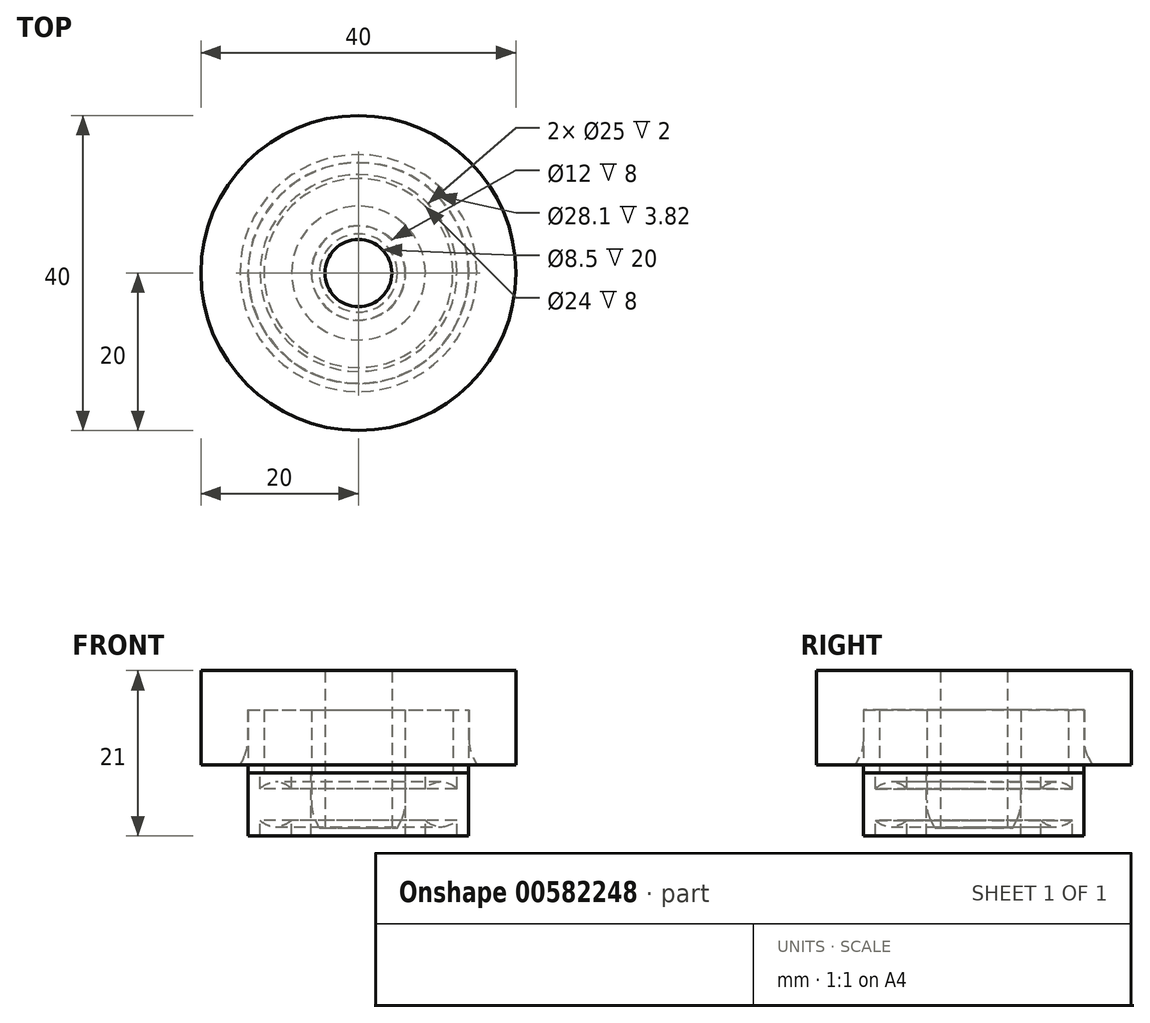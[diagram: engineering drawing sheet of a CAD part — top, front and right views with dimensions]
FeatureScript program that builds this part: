
annotation { "Feature Type Name" : "Feature", "Feature Type Description" : "" }
export const myFeature = defineFeature(function(context is Context, id is Id, definition is map)
    precondition{}
    {
        {
            var Q0;
            Q0=qCreatedBy(makeId("Front.planeOp"),FACE);
            var sketch = newSketch(context, id + "F0", { "sketchPlane" : qUnion([Q0])});
            skLineSegment(sketch, "E0", {"start": v(0, 0) * mm, "end": v(0, 32.04) * mm, "construction": true});
            skLineSegment(sketch, "E1.bottom", {"start": v(12, 0) * mm, "end": v(14, 0) * mm});
            skLineSegment(sketch, "E1.top", {"start": v(12, 8) * mm, "end": v(14, 8) * mm});
            skLineSegment(sketch, "E1.left", {"start": v(12, 0) * mm, "end": v(12, 8) * mm});
            skLineSegment(sketch, "E1.right", {"start": v(14, 0) * mm, "end": v(14, 8) * mm});
            skSolve(sketch);
        }
        {
            var Q0;
            Q0 = qSketchRegion(id + "F0", true);
            var Q1;
            Q1=sQuery(id+"F0.wireOp",EDGE,"E0");
            revolve(context, id + "F1", {"entities" : qUnion([Q0]), "axis" : qUnion([Q1]), "revolveType" : RevolveType.FULL});
        }
        {
            var Q0;
            Q0=qCreatedBy(makeId("Front.planeOp"),FACE);
            var sketch = newSketch(context, id + "F2", { "sketchPlane" : qUnion([Q0])});
            skLineSegment(sketch, "E2", {"start": v(0, 0) * mm, "end": v(0, 16.36) * mm, "construction": true});
            skLineSegment(sketch, "E3", {"start": v(14.05, 1) * mm, "end": v(20, 1) * mm});
            skLineSegment(sketch, "E4", {"start": v(20, 1) * mm, "end": v(20, 13) * mm});
            skLineSegment(sketch, "E5", {"start": v(20, 13) * mm, "end": v(4.25, 13) * mm});
            skLineSegment(sketch, "E6", {"start": v(4.25, 13) * mm, "end": v(4.25, -7) * mm});
            skLineSegment(sketch, "E7", {"start": v(4.25, -7) * mm, "end": v(5.95, -7) * mm});
            skLineSegment(sketch, "E8", {"start": v(5.95, -7) * mm, "end": v(5.95, 8) * mm});
            skLineSegment(sketch, "E9", {"start": v(5.95, 8) * mm, "end": v(14.05, 8) * mm});
            skLineSegment(sketch, "E10", {"start": v(14.05, 8) * mm, "end": v(14.05, 1) * mm});
            skSolve(sketch);
        }
        {
            var Q0;
            Q0 = qSketchRegion(id + "F2", true);
            var Q1;
            Q1=sQuery(id+"F2.wireOp",EDGE,"E2");
            revolve(context, id + "F3", {"entities" : qUnion([Q0]), "axis" : qUnion([Q1]), "revolveType" : RevolveType.FULL});
        }
        {
            var Q0;
            Q0=qCreatedBy(makeId("Front.planeOp"),FACE);
            var sketch = newSketch(context, id + "F4", { "sketchPlane" : qUnion([Q0])});
            skLineSegment(sketch, "E11", {"start": v(0, 0) * mm, "end": v(0, -20.8) * mm, "construction": true});
            skLineSegment(sketch, "E12", {"start": v(14, 0) * mm, "end": v(14, -8) * mm});
            skLineSegment(sketch, "E13", {"start": v(14, -8) * mm, "end": v(12.5, -8) * mm});
            skLineSegment(sketch, "E14", {"start": v(12.5, -8) * mm, "end": v(12.5, -6) * mm});
            skLineSegment(sketch, "E15", {"start": v(12.5, -6) * mm, "end": v(8.5, -6) * mm, "construction": true});
            skLineSegment(sketch, "E16", {"start": v(8.5, -6) * mm, "end": v(8.5, -8) * mm});
            skLineSegment(sketch, "E17", {"start": v(8.5, -8) * mm, "end": v(6, -8) * mm});
            skLineSegment(sketch, "E18", {"start": v(6, -8) * mm, "end": v(6, 0) * mm});
            skLineSegment(sketch, "E19", {"start": v(6, 0) * mm, "end": v(8.5, 0) * mm});
            skLineSegment(sketch, "E20", {"start": v(8.5, 0) * mm, "end": v(8.5, -2) * mm});
            skLineSegment(sketch, "E21", {"start": v(8.5, -2) * mm, "end": v(12.5, -2) * mm, "construction": true});
            skLineSegment(sketch, "E22", {"start": v(12.5, -2) * mm, "end": v(12.5, 0) * mm});
            skLineSegment(sketch, "E23", {"start": v(12.5, 0) * mm, "end": v(14, 0) * mm});
            skCircle(sketch, "E24", {"center": v(10.5, -4) * mm, "radius": 2.83 * mm, "construction": true});
            skArc(sketch, "E25", {"start": v(8.5, -2) * mm, "mid": v(10.5, -1.17) * mm, "end": v(12.5, -2) * mm});
            skArc(sketch, "E26", {"start": v(12.5, -6) * mm, "mid": v(10.5, -6.83) * mm, "end": v(8.5, -6) * mm});
            skSolve(sketch);
        }
        {
            var Q0;
            Q0 = qSketchRegion(id + "F4", true);
            var Q1;
            Q1=sQuery(id+"F4.wireOp",EDGE,"E11");
            revolve(context, id + "F5", {"entities" : qUnion([Q0]), "axis" : qUnion([Q1]), "revolveType" : RevolveType.FULL});
        }
        {
            var Q0;
            Q0=makeQuery(id+"F3.opRevolve","SWEPT_EDGE",EDGE,{"disambiguationData":[OSD([sQuery(id+"F2.wireOp",EDGE,"E3"),sQuery(id+"F2.wireOp",EDGE,"E10")])]});
            chamfer(context, id + "F6", {"entities" : qUnion([Q0]), "chamferType" : ChamferType.TWO_OFFSETS, "width1" : 2 * mm, "oppositeDirection" : false, "width2" : 1 * mm, "tangentPropagation" : true});
        }
        {
            var Q0;
            Q0=makeQuery(id+"F3.opRevolve","SWEPT_EDGE",EDGE,{"disambiguationData":[OSD([sQuery(id+"F2.wireOp",EDGE,"E7"),sQuery(id+"F2.wireOp",EDGE,"E8")])]});
            chamfer(context, id + "F7", {"entities" : qUnion([Q0]), "chamferType" : ChamferType.TWO_OFFSETS, "width1" : 1 * mm, "oppositeDirection" : false, "width2" : 2 * mm, "tangentPropagation" : true});
        }
        {
            var Q0;
            {var subQ0=sQuery(id+"F2.wireOp",EDGE,"E10");Q0=makeQuery(id+"F6.opChamfer","BLEND_EDGE",EDGE,{"blendedFrom":[makeQuery(id+"F3.opRevolve","SWEPT_EDGE",EDGE,{"disambiguationData":[OSD([sQuery(id+"F2.wireOp",EDGE,"E3"),subQ0])]}),makeQuery(id+"F3.opRevolve","SWEPT_FACE",FACE,{"disambiguationData":[OSD([subQ0])]})],"blendedInto":[makeQuery(id+"F3.opRevolve","SWEPT_FACE",FACE,{"disambiguationData":[OSD([subQ0])]})]});}
            var Q1;
            {var subQ0=sQuery(id+"F2.wireOp",EDGE,"E8");Q1=makeQuery(id+"F7.opChamfer","BLEND_EDGE",EDGE,{"blendedFrom":[makeQuery(id+"F3.opRevolve","SWEPT_EDGE",EDGE,{"disambiguationData":[OSD([sQuery(id+"F2.wireOp",EDGE,"E7"),subQ0])]}),makeQuery(id+"F3.opRevolve","SWEPT_FACE",FACE,{"disambiguationData":[OSD([subQ0])]})],"blendedInto":[makeQuery(id+"F3.opRevolve","SWEPT_FACE",FACE,{"disambiguationData":[OSD([subQ0])]})]});}
            fillet(context, id + "F8", {"entities" : qUnion([Q0, Q1]), "radius" : 5 * mm, "tangentPropagation" : true, "allowEdgeOverflow" : false});
        }
    });
